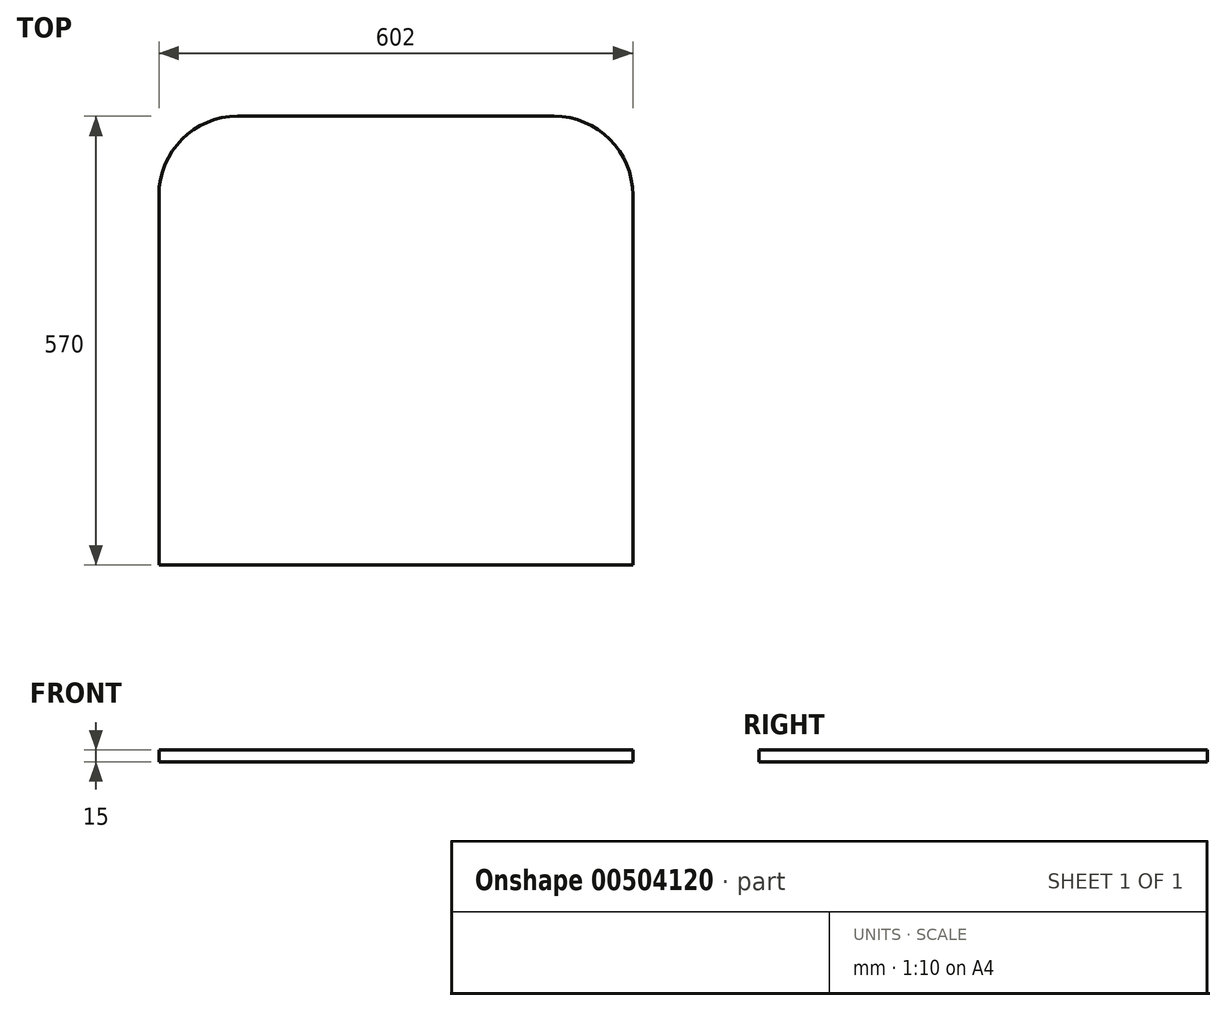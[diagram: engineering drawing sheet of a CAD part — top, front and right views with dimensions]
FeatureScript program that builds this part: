
annotation { "Feature Type Name" : "Feature", "Feature Type Description" : "" }
export const myFeature = defineFeature(function(context is Context, id is Id, definition is map)
    precondition{}
    {
        {
            var Q0;
            Q0=qCreatedBy(makeId("Top.planeOp"),FACE);
            var sketch = newSketch(context, id + "F0", { "sketchPlane" : qUnion([Q0])});
            skLineSegment(sketch, "E0", {"start": v(0, 0) * mm, "end": v(602, 0) * mm});
            skLineSegment(sketch, "E1", {"start": v(602, 0) * mm, "end": v(602, 570) * mm});
            skLineSegment(sketch, "E2", {"start": v(602, 570) * mm, "end": v(0, 570) * mm});
            skLineSegment(sketch, "E3", {"start": v(0, 570) * mm, "end": v(0, 0) * mm});
            skPoint(sketch, "E4.orphan", {"position": v(602, 0) * mm});
            skSolve(sketch);
        }
        {
            var Q0;
            Q0=makeQuery(id+"F0.imprint","IMPRINT",FACE,{"disambiguationData":[TD([[makeQuery(id+"F0.imprint","IMPRINT",EDGE,{"derivedFrom":sQuery(id+"F0.wireOp",EDGE,"E0")}),1.0]])]});
            extrude(context, id + "F1", {"entities" : qUnion([Q0]), "depth" : 15 * mm});
        }
        {
            var Q0;
            Q0=makeQuery(id+"F1.opExtrude","SWEPT_EDGE",EDGE,{"disambiguationData":[OSD([sQuery(id+"F0.wireOp",EDGE,"E2"),sQuery(id+"F0.wireOp",EDGE,"E3")])]});
            var Q1;
            Q1=makeQuery(id+"F1.opExtrude","SWEPT_EDGE",EDGE,{"disambiguationData":[OSD([sQuery(id+"F0.wireOp",EDGE,"E1"),sQuery(id+"F0.wireOp",EDGE,"E2")])]});
            fillet(context, id + "F2", {"entities" : qUnion([Q0, Q1]), "radius" : 100 * mm, "tangentPropagation" : true, "allowEdgeOverflow" : false});
        }
    });
